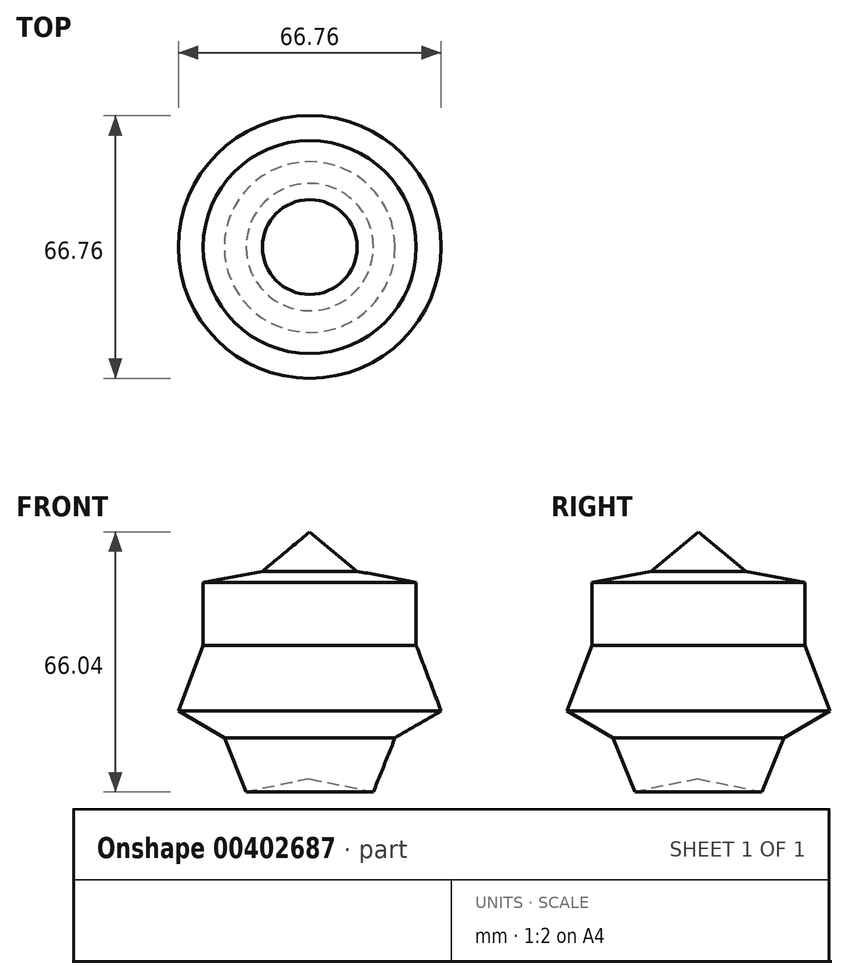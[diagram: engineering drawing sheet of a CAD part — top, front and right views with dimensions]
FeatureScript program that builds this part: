
annotation { "Feature Type Name" : "Feature", "Feature Type Description" : "" }
export const myFeature = defineFeature(function(context is Context, id is Id, definition is map)
    precondition{}
    {
        {
            var Q0;
            Q0=qCreatedBy(makeId("Front.planeOp"),FACE);
            var sketch = newSketch(context, id + "F0", { "sketchPlane" : qUnion([Q0])});
            skPoint(sketch, "E0.0.midPoint", {"position": v(-10.85, -22.52) * mm});
            skLineSegment(sketch, "E1", {"start": v(-27.05, 6.17) * mm, "end": v(-27.05, 22.2) * mm});
            skLineSegment(sketch, "E2", {"start": v(-27.05, 22.2) * mm, "end": v(-12.04, 25) * mm});
            skLineSegment(sketch, "E3", {"start": v(-12.04, 25) * mm, "end": v(0, 35) * mm});
            skPoint(sketch, "E4.endSnap0", {"position": v(-19.55, 23.6) * mm});
            skLineSegment(sketch, "E5", {"start": v(0, -27.75) * mm, "end": v(-16.17, -31.04) * mm});
            skLineSegment(sketch, "E6", {"start": v(-16.17, -31.04) * mm, "end": v(-21.7, -17.3) * mm});
            skLineSegment(sketch, "E7", {"start": v(-27.05, 6.17) * mm, "end": v(-33.38, -10.51) * mm});
            skLineSegment(sketch, "E8", {"start": v(-33.38, -10.51) * mm, "end": v(-21.7, -17.3) * mm});
            skPoint(sketch, "E4.end.orphan", {"position": v(25.84, 23.6) * mm});
            skLineSegment(sketch, "E9", {"start": v(0, 35) * mm, "end": v(0, -27.75) * mm});
            skSolve(sketch);
        }
        {
            var Q0;
            Q0 = qSketchRegion(id + "F0", true);
            var Q1;
            Q1=sQuery(id+"F0.wireOp",EDGE,"E9");
            revolve(context, id + "F1", {"entities" : qUnion([Q0]), "axis" : qUnion([Q1]), "revolveType" : RevolveType.FULL});
        }
    });
